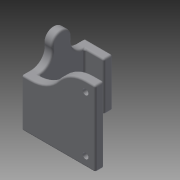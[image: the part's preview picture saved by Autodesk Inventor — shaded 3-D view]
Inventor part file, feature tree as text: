
AUTODESK INVENTOR PART (.ipt)
format: ipt  version: 2013 (Build 170138000, 138)  size: 256,000 bytes
history: native  units: mm
features: extrude x5, sketch x5, fillet x1
ambient origin geometry x8: Origin, YZ Plane, XZ Plane, XY Plane, X Axis, Y Axis, Z Axis, Center Point
bodies: Solid1 (feature_tree)
feature tree (11):
  extrude  "Extrusion1"  Depth=5.0mm
  extrude  "Extrusion2"  Depth=36.4mm
  extrude  "Extrusion3"  Depth=31.0mm
  extrude  "Extrusion4"  Depth=3.2mm
  extrude  "Extrusion5"  Depth=42.0mm TaperAngle=0.0deg
  fillet  "Fillet4"  Radius=15.0mm
  sketch  "Sketch1"  dims[d0=5.0mm d2=5.0mm]
  sketch  "Sketch2"  dims[d3=25.4mm d4=36.4mm]
  sketch  "Sketch3"  dims[d5=42.0mm d6=0.0mm d9=31.0mm]
  sketch  "Sketch4"  dims[d11=35.9mm d12=3.2mm]
  sketch  "Sketch5"  dims[d13=3.2mm d14=42.0mm d15=0.0mm d17=15.0mm d19=5.0mm d20=5.0mm d21=0.0mm d22=7.5mm d25=5.0mm d26=0.0mm d27=5.0mm d28=0.0mm d29=1.0mm]
